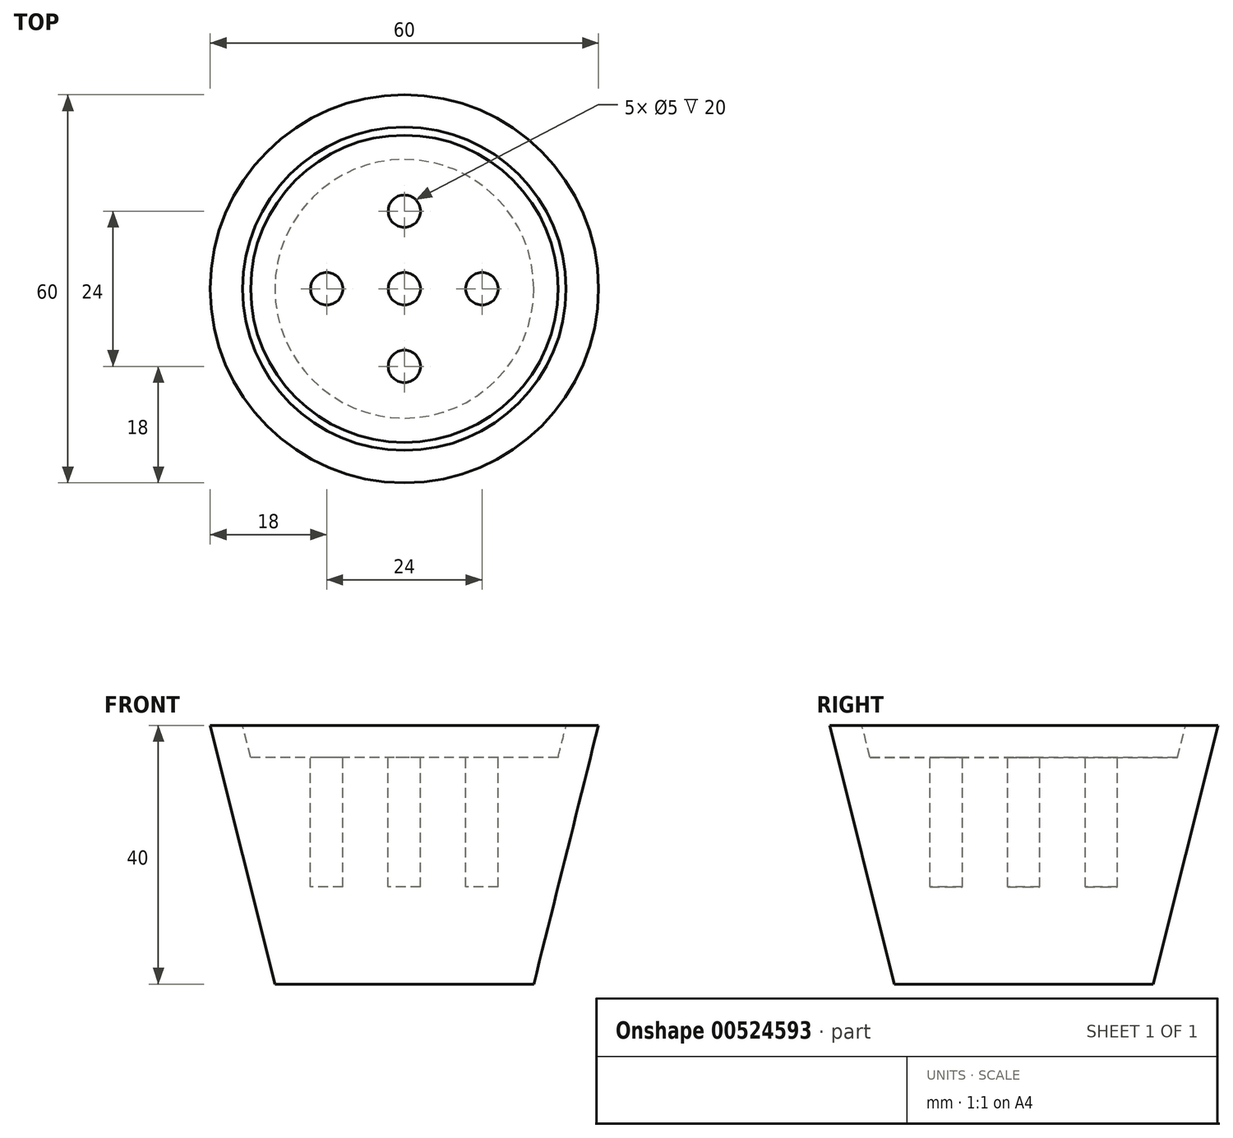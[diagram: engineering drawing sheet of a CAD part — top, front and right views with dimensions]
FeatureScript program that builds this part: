
annotation { "Feature Type Name" : "Feature", "Feature Type Description" : "" }
export const myFeature = defineFeature(function(context is Context, id is Id, definition is map)
    precondition{}
    {
        {
            var Q0;
            Q0=qCreatedBy(makeId("Front.planeOp"),FACE);
            var sketch = newSketch(context, id + "F0", { "sketchPlane" : qUnion([Q0])});
            skLineSegment(sketch, "E0", {"start": v(20, 0) * mm, "end": v(30, 40) * mm});
            skLineSegment(sketch, "E1", {"start": v(30, 40) * mm, "end": v(25, 40) * mm});
            skLineSegment(sketch, "E2", {"start": v(25, 40) * mm, "end": v(23.75, 35) * mm});
            skLineSegment(sketch, "E3", {"start": v(23.75, 35) * mm, "end": v(0, 35) * mm});
            skLineSegment(sketch, "E4", {"start": v(0, 35) * mm, "end": v(0, 0) * mm});
            skLineSegment(sketch, "E5", {"start": v(0, 0) * mm, "end": v(20, 0) * mm});
            skSolve(sketch);
        }
        {
            var Q0;
            Q0=makeQuery(id+"F0.imprint","IMPRINT",FACE,{"disambiguationData":[TD([[makeQuery(id+"F0.imprint","IMPRINT",EDGE,{"derivedFrom":sQuery(id+"F0.wireOp",EDGE,"E0")}),1.0]])]});
            var Q1;
            Q1=sQuery(id+"F0.wireOp",EDGE,"E4");
            revolve(context, id + "F1", {"entities" : qUnion([Q0]), "axis" : qUnion([Q1]), "revolveType" : RevolveType.FULL});
        }
        {
            var Q0;
            Q0=makeQuery(id+"F1.opRevolve","SWEPT_FACE",FACE,{"disambiguationData":[OSD([sQuery(id+"F0.wireOp",EDGE,"E3")])]});
            var sketch = newSketch(context, id + "F2", { "sketchPlane" : qUnion([Q0])});
            skCircle(sketch, "E6", {"center": v(0, 0) * mm, "radius": 2.5 * mm});
            skCircle(sketch, "E7", {"center": v(0, 12) * mm, "radius": 2.5 * mm});
            skCircle(sketch, "E8.1.0", {"center": v(-12, 0) * mm, "radius": 2.5 * mm});
            skCircle(sketch, "E8.2.0", {"center": v(0, -12) * mm, "radius": 2.5 * mm});
            skCircle(sketch, "E8.3.0", {"center": v(12, 0) * mm, "radius": 2.5 * mm});
            skSolve(sketch);
        }
        {
            var Q0;
            Q0=makeQuery(id+"F2.imprint","IMPRINT",FACE,{"disambiguationData":[TD([[makeQuery(id+"F2.imprint","IMPRINT",EDGE,{"derivedFrom":sQuery(id+"F2.wireOp",EDGE,"E8.3.0")}),1.0]])]});
            var Q1;
            Q1=makeQuery(id+"F2.imprint","IMPRINT",FACE,{"disambiguationData":[TD([[makeQuery(id+"F2.imprint","IMPRINT",EDGE,{"derivedFrom":sQuery(id+"F2.wireOp",EDGE,"E8.2.0")}),1.0]])]});
            var Q2;
            Q2=makeQuery(id+"F2.imprint","IMPRINT",FACE,{"disambiguationData":[TD([[makeQuery(id+"F2.imprint","IMPRINT",EDGE,{"derivedFrom":sQuery(id+"F2.wireOp",EDGE,"E6")}),1.0]])]});
            var Q3;
            Q3=makeQuery(id+"F2.imprint","IMPRINT",FACE,{"disambiguationData":[TD([[makeQuery(id+"F2.imprint","IMPRINT",EDGE,{"derivedFrom":sQuery(id+"F2.wireOp",EDGE,"E8.1.0")}),1.0]])]});
            var Q4;
            Q4=makeQuery(id+"F2.imprint","IMPRINT",FACE,{"disambiguationData":[TD([[makeQuery(id+"F2.imprint","IMPRINT",EDGE,{"derivedFrom":sQuery(id+"F2.wireOp",EDGE,"E7")}),1.0]])]});
            var Q5;
            Q5=sQuery(id+"F2.wireOp",EDGE,"E8.3.0");
            var Q6;
            Q6=sQuery(id+"F2.wireOp",EDGE,"E6");
            var Q7;
            Q7=sQuery(id+"F2.wireOp",EDGE,"E8.2.0");
            var Q8;
            Q8=sQuery(id+"F2.wireOp",EDGE,"E8.1.0");
            var Q9;
            Q9=sQuery(id+"F2.wireOp",EDGE,"E7");
            extrude(context, id + "F3", {"entities" : qUnion([Q0, Q1, Q2, Q3, Q4]), "operationType" : NewBodyOperationType.REMOVE, "surfaceEntities" : qUnion([Q5, Q6, Q7, Q8, Q9]), "oppositeDirection" : true, "depth" : 20 * mm, "offsetDistance" : 25 * mm});
        }
    });
